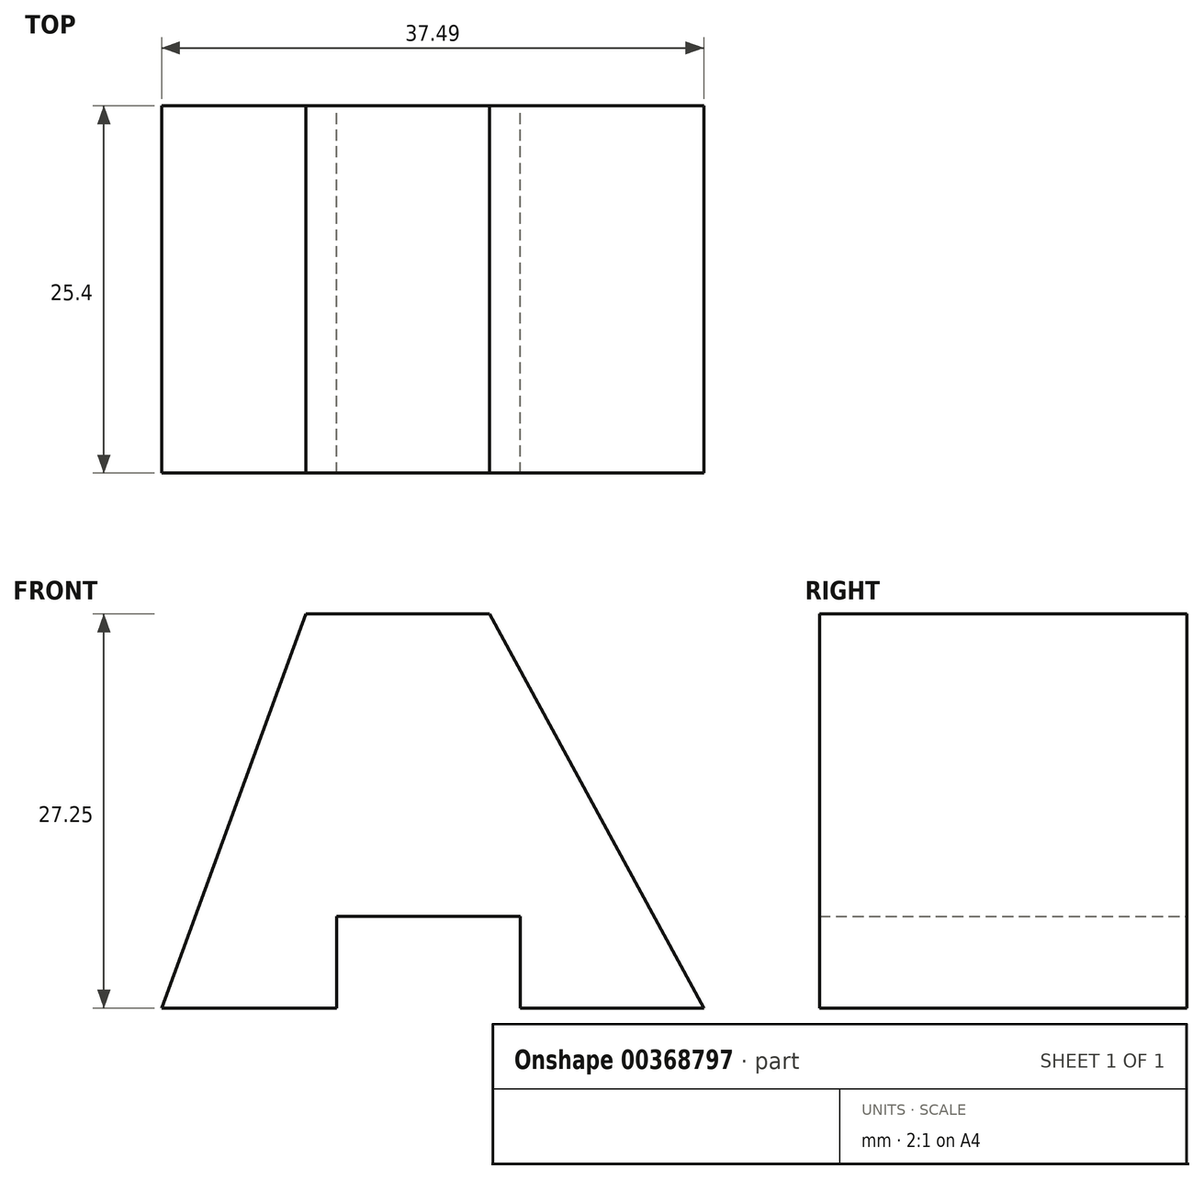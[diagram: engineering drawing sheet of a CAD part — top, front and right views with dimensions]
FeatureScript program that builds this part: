
annotation { "Feature Type Name" : "Feature", "Feature Type Description" : "" }
export const myFeature = defineFeature(function(context is Context, id is Id, definition is map)
    precondition{}
    {
        {
            var Q0;
            Q0=qCreatedBy(makeId("Front.planeOp"),FACE);
            var sketch = newSketch(context, id + "F0", { "sketchPlane" : qUnion([Q0])});
            skLineSegment(sketch, "E0", {"start": v(0, -1.68) * mm, "end": v(10.58, 27.25) * mm});
            skLineSegment(sketch, "E1", {"start": v(10.58, 27.25) * mm, "end": v(23.28, 27.25) * mm});
            skLineSegment(sketch, "E2", {"start": v(23.28, 27.25) * mm, "end": v(38.1, 0) * mm});
            skLineSegment(sketch, "E3", {"start": v(38.1, 0) * mm, "end": v(25.4, 0) * mm});
            skLineSegment(sketch, "E4", {"start": v(25.4, 0) * mm, "end": v(25.4, 6.35) * mm});
            skLineSegment(sketch, "E5", {"start": v(25.4, 6.35) * mm, "end": v(12.7, 6.35) * mm});
            skLineSegment(sketch, "E6", {"start": v(12.7, 6.35) * mm, "end": v(12.7, 0) * mm});
            skLineSegment(sketch, "E7", {"start": v(12.7, 0) * mm, "end": v(0, 0) * mm});
            skSolve(sketch);
        }
        {
            var Q0;
            {var subQ0=sQuery(id+"F0.wireOp",EDGE,"E1");Q0=makeQuery(id+"F0.imprint","IMPRINT",FACE,{"disambiguationData":[TD([[makeQuery(id+"F0.imprint","IMPRINT",EDGE,{"derivedFrom":subQ0}),-1.0]])]});}
            extrude(context, id + "F1", {"entities" : qUnion([Q0]), "depth" : 25.4 * mm});
        }
    });
